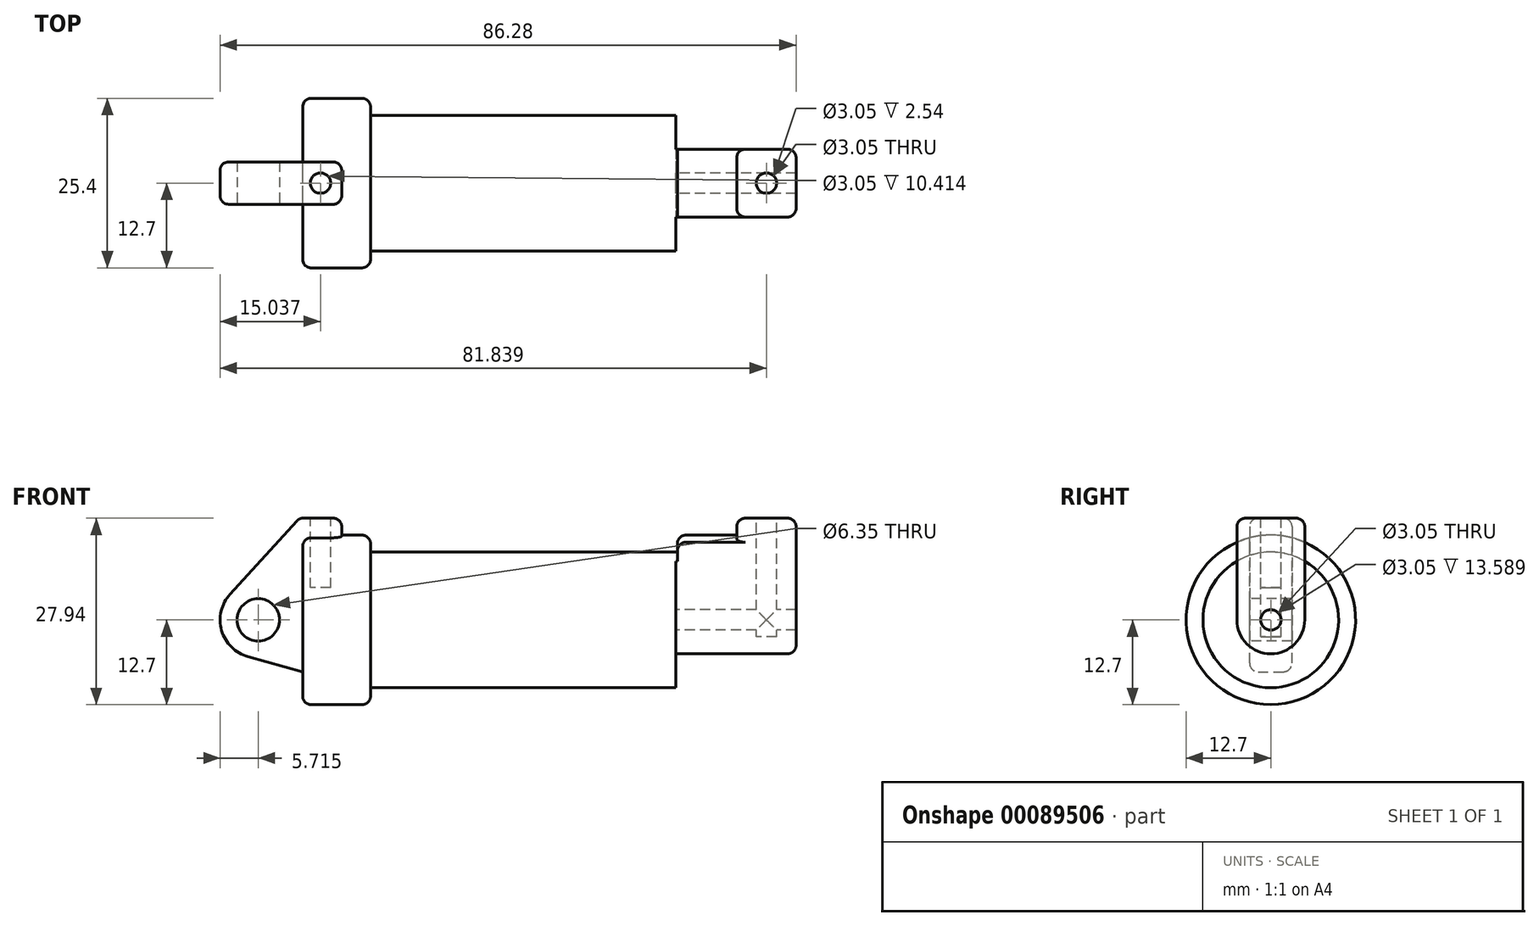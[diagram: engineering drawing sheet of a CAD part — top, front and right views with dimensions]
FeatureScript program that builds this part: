
annotation { "Feature Type Name" : "Feature", "Feature Type Description" : "" }
export const myFeature = defineFeature(function(context is Context, id is Id, definition is map)
    precondition{}
    {
        {
            var Q0;
            Q0=qCreatedBy(makeId("Front.planeOp"),FACE);
            var sketch = newSketch(context, id + "F0", { "sketchPlane" : qUnion([Q0])});
            skLineSegment(sketch, "E0", {"start": v(0, 0) * mm, "end": v(0, 12.7) * mm});
            skLineSegment(sketch, "E1", {"start": v(0, 12.7) * mm, "end": v(10.16, 12.7) * mm});
            skLineSegment(sketch, "E2", {"start": v(10.16, 12.7) * mm, "end": v(10.16, 10.16) * mm});
            skLineSegment(sketch, "E3", {"start": v(10.16, 10.16) * mm, "end": v(56.13, 10.16) * mm});
            skLineSegment(sketch, "E4", {"start": v(56.13, 10.16) * mm, "end": v(56.13, 12.7) * mm});
            skLineSegment(sketch, "E5", {"start": v(56.13, 12.7) * mm, "end": v(66.3, 12.7) * mm});
            skLineSegment(sketch, "E6", {"start": v(66.3, 12.7) * mm, "end": v(66.3, 0) * mm});
            skLineSegment(sketch, "E7", {"start": v(66.3, 0) * mm, "end": v(0, 0) * mm});
            skLineSegment(sketch, "E8", {"start": v(5.84, 15.24) * mm, "end": v(-0.5, 15.24) * mm});
            skLineSegment(sketch, "E9", {"start": v(-0.5, 15.24) * mm, "end": v(-10.88, 3.85) * mm});
            skLineSegment(sketch, "E10", {"start": v(0, 0) * mm, "end": v(-6.65, 0) * mm});
            skCircle(sketch, "E11", {"center": v(-6.65, 0) * mm, "radius": 5.72 * mm});
            skCircle(sketch, "E12", {"center": v(-6.65, 0) * mm, "radius": 3.18 * mm});
            skLineSegment(sketch, "E13", {"start": v(5.84, 15.24) * mm, "end": v(5.84, -9.4) * mm});
            skLineSegment(sketch, "E14", {"start": v(5.84, -9.4) * mm, "end": v(-8.18, -5.5) * mm});
            skSolve(sketch);
        }
        {
            var Q0;
            {var subQ0=sQuery(id+"F0.wireOp",EDGE,"E0");Q0=makeQuery(id+"F0.imprint","IMPRINT",FACE,{"disambiguationData":[TD([[makeQuery(id+"F0.imprint","IMPRINT",EDGE,{"derivedFrom":subQ0}),-1.0]])]});}
            var Q1;
            {var subQ3=sQuery(id+"F0.wireOp",EDGE,"E0");Q1=makeQuery(id+"F0.imprint","IMPRINT",FACE,{"disambiguationData":[TD([[makeQuery(id+"F0.imprint","IMPRINT",EDGE,{"derivedFrom":subQ3}),1.0]])]});}
            var Q2;
            {var subQ0=sQuery(id+"F0.wireOp",EDGE,"E14");Q2=makeQuery(id+"F0.imprint","IMPRINT",FACE,{"disambiguationData":[TD([[makeQuery(id+"F0.imprint","IMPRINT",EDGE,{"derivedFrom":subQ0}),-1.0]])]});}
            var Q3;
            {var subQ4=sQuery(id+"F0.wireOp",EDGE,"E12");Q3=makeQuery(id+"F0.imprint","IMPRINT",FACE,{"disambiguationData":[TD([[makeQuery(id+"F0.imprint","IMPRINT",EDGE,{"derivedFrom":subQ4}),-1.0]])]});}
            extrude(context, id + "F1", {"entities" : qUnion([Q0, Q1, Q2, Q3]), "endBound" : BoundingType.SYMMETRIC, "oppositeDirection" : true, "depth" : 6.35 * mm});
        }
        {
            var Q0;
            {var subQ0=sQuery(id+"F0.wireOp",EDGE,"E2");Q0=makeQuery(id+"F0.imprint","IMPRINT",FACE,{"disambiguationData":[TD([[makeQuery(id+"F0.imprint","IMPRINT",EDGE,{"derivedFrom":subQ0}),-1.0]])]});}
            var Q1;
            {var subQ0=sQuery(id+"F0.wireOp",EDGE,"E0");Q1=makeQuery(id+"F0.imprint","IMPRINT",FACE,{"disambiguationData":[TD([[makeQuery(id+"F0.imprint","IMPRINT",EDGE,{"derivedFrom":subQ0}),-1.0]])]});}
            var Q2;
            Q2=sQuery(id+"F0.wireOp",EDGE,"E7");
            revolve(context, id + "F2", {"operationType" : NewBodyOperationType.ADD, "entities" : qUnion([Q0, Q1]), "axis" : qUnion([Q2]), "revolveType" : RevolveType.FULL});
        }
        {
            var Q0;
            Q0=makeQuery(id+"F2.opRevolve","SWEPT_FACE",FACE,{"disambiguationData":[OSD([sQuery(id+"F0.wireOp",EDGE,"E6")])]});
            var sketch = newSketch(context, id + "F3", { "sketchPlane" : qUnion([Q0])});
            skCircle(sketch, "E15", {"center": v(0, 0) * mm, "radius": 1.52 * mm});
            skCircle(sketch, "E16", {"center": v(0, 0) * mm, "radius": 5.08 * mm});
            skLineSegment(sketch, "E17", {"start": v(-5.08, 0) * mm, "end": v(-5.08, 15.24) * mm});
            skLineSegment(sketch, "E18", {"start": v(5.08, 0) * mm, "end": v(5.08, 15.24) * mm});
            skLineSegment(sketch, "E19", {"start": v(-5.08, 15.24) * mm, "end": v(5.08, 15.24) * mm});
            skSolve(sketch);
        }
        {
            var Q0;
            Q0 = qSketchRegion(id + "F3", true);
            extrude(context, id + "F4", {"entities" : qUnion([Q0]), "operationType" : NewBodyOperationType.ADD, "depth" : 7.62 * mm});
        }
        {
            var Q0;
            Q0 = qSketchRegion(id + "F3", true);
            extrude(context, id + "F5", {"entities" : qUnion([Q0]), "operationType" : NewBodyOperationType.ADD, "oppositeDirection" : true, "depth" : 1.27 * mm});
        }
        {
            var Q0;
            {var subQ0=sQuery(id+"F3.wireOp",EDGE,"E19");Q0=makeQuery(id+"F5.boolean.opBoolean","MERGE",FACE,{"derivedFrom":[makeQuery(id+"F4.opExtrude","SWEPT_FACE",FACE,{"disambiguationData":[OSD([subQ0])]}),makeQuery(id+"F5.opExtrude","SWEPT_FACE",FACE,{"disambiguationData":[OSD([subQ0])]})]});}
            var sketch = newSketch(context, id + "F6", { "sketchPlane" : qUnion([Q0])});
            skLineSegment(sketch, "E20", {"start": v(65.02, 0) * mm, "end": v(73.91, 0) * mm, "construction": true});
            skLineSegment(sketch, "E21", {"start": v(69.47, 5.08) * mm, "end": v(69.47, -5.08) * mm, "construction": true});
            skCircle(sketch, "E22", {"center": v(69.47, 0) * mm, "radius": 1.52 * mm});
            skSolve(sketch);
        }
        {
            var Q0;
            Q0=makeQuery(id+"F4.boolean.opBoolean","SPLIT",FACE,{"disambiguationData":[TD([makeQuery(id+"F4.opExtrude","SWEPT_FACE",FACE,{"disambiguationData":[OSD([sQuery(id+"F3.wireOp",EDGE,"E15")])]})])],"derivedFrom":makeQuery(id+"F2.opRevolve","SWEPT_FACE",FACE,{"disambiguationData":[OSD([sQuery(id+"F0.wireOp",EDGE,"E6")])]})});
            extrude(context, id + "F7", {"entities" : qUnion([Q0]), "operationType" : NewBodyOperationType.ADD, "oppositeDirection" : true, "depth" : 10.4 * mm});
        }
        {
            var Q0;
            Q0=makeQuery(id+"F6.imprint","IMPRINT",FACE,{"disambiguationData":[TD([[makeQuery(id+"F6.imprint","IMPRINT",EDGE,{"derivedFrom":sQuery(id+"F6.wireOp",EDGE,"E22")}),1.0]])]});
            extrude(context, id + "F8", {"entities" : qUnion([Q0]), "operationType" : NewBodyOperationType.REMOVE, "oppositeDirection" : true, "depth" : 17.78 * mm});
        }
        {
            var Q0;
            Q0=makeQuery(id+"F4.boolean.opBoolean","SPLIT",FACE,{"disambiguationData":[TD([makeQuery(id+"F4.opExtrude","SWEPT_FACE",FACE,{"disambiguationData":[OSD([sQuery(id+"F3.wireOp",EDGE,"E15")])]})])],"derivedFrom":makeQuery(id+"F2.opRevolve","SWEPT_FACE",FACE,{"disambiguationData":[OSD([sQuery(id+"F0.wireOp",EDGE,"E6")])]})});
            extrude(context, id + "F9", {"entities" : qUnion([Q0]), "operationType" : NewBodyOperationType.REMOVE, "oppositeDirection" : true, "depth" : 10.4 * mm});
        }
        {
            var Q0;
            Q0=makeQuery(id+"F1.opExtrude","SWEPT_FACE",FACE,{"disambiguationData":[OSD([sQuery(id+"F0.wireOp",EDGE,"E8")])]});
            var sketch = newSketch(context, id + "F10", { "sketchPlane" : qUnion([Q0])});
            skLineSegment(sketch, "E23", {"start": v(2.67, 3.18) * mm, "end": v(2.67, -3.18) * mm, "construction": true});
            skLineSegment(sketch, "E24", {"start": v(-0.5, 0) * mm, "end": v(5.84, 0) * mm, "construction": true});
            skCircle(sketch, "E25", {"center": v(2.67, 0) * mm, "radius": 1.52 * mm});
            skSolve(sketch);
        }
        {
            var Q0;
            Q0 = qSketchRegion(id + "F10", true);
            extrude(context, id + "F11", {"entities" : qUnion([Q0]), "operationType" : NewBodyOperationType.REMOVE, "oppositeDirection" : true, "depth" : 10.4 * mm});
        }
        {
            var Q0;
            Q0=makeQuery(id+"F2.opRevolve","SWEPT_EDGE",EDGE,{"disambiguationData":[OSD([sQuery(id+"F0.wireOp",EDGE,"E1"),sQuery(id+"F0.wireOp",EDGE,"E2")])]});
            var Q1;
            Q1=makeQuery(id+"F2.opRevolve","SWEPT_EDGE",EDGE,{"disambiguationData":[OSD([sQuery(id+"F0.wireOp",EDGE,"E0"),sQuery(id+"F0.wireOp",EDGE,"E1")])]});
            var Q2;
            Q2=makeQuery(id+"F4.boolean.opBoolean","SPLIT",EDGE,{"disambiguationData":[OD(1.0)],"derivedFrom":makeQuery(id+"F2.opRevolve","SWEPT_EDGE",EDGE,{"disambiguationData":[OSD([sQuery(id+"F0.wireOp",EDGE,"E5"),sQuery(id+"F0.wireOp",EDGE,"E6")])]})});
            var Q3;
            Q3=makeQuery(id+"F2.opRevolve","SWEPT_EDGE",EDGE,{"disambiguationData":[OSD([sQuery(id+"F0.wireOp",EDGE,"E4"),sQuery(id+"F0.wireOp",EDGE,"E5")])]});
            fillet(context, id + "F12", {"entities" : qUnion([Q0, Q1, Q2, Q3]), "radius" : 1.27 * mm, "tangentPropagation" : true, "allowEdgeOverflow" : false});
        }
        {
            var Q0;
            {var subQ0=sQuery(id+"F3.wireOp",EDGE,"E19");var subQ1=sQuery(id+"F3.wireOp",EDGE,"E17");Q0=makeQuery(id+"F5.boolean.opBoolean","MERGE",EDGE,{"derivedFrom":[makeQuery(id+"F4.opExtrude","SWEPT_EDGE",EDGE,{"disambiguationData":[OSD([subQ1,subQ0])]}),makeQuery(id+"F5.opExtrude","SWEPT_EDGE",EDGE,{"disambiguationData":[OSD([subQ1,subQ0])]})]});}
            var Q1;
            Q1=makeQuery(id+"F4.opExtrude","CAP_EDGE",EDGE,{"disambiguationData":[OSD([sQuery(id+"F3.wireOp",EDGE,"E19")])],"isStart":false});
            var Q2;
            Q2=makeQuery(id+"F5.opExtrude","CAP_EDGE",EDGE,{"disambiguationData":[OSD([sQuery(id+"F3.wireOp",EDGE,"E19")])],"isStart":false});
            var Q3;
            {var subQ0=sQuery(id+"F3.wireOp",EDGE,"E19");var subQ1=sQuery(id+"F3.wireOp",EDGE,"E18");Q3=makeQuery(id+"F5.boolean.opBoolean","MERGE",EDGE,{"derivedFrom":[makeQuery(id+"F4.opExtrude","SWEPT_EDGE",EDGE,{"disambiguationData":[OSD([subQ1,subQ0])]}),makeQuery(id+"F5.opExtrude","SWEPT_EDGE",EDGE,{"disambiguationData":[OSD([subQ1,subQ0])]})]});}
            var Q4;
            Q4=makeQuery(id+"F4.opExtrude","CAP_EDGE",EDGE,{"disambiguationData":[OSD([sQuery(id+"F3.wireOp",EDGE,"E18")])],"isStart":false});
            var Q5;
            Q5=makeQuery(id+"F5.opExtrude","CAP_EDGE",EDGE,{"disambiguationData":[OSD([sQuery(id+"F3.wireOp",EDGE,"E18")])],"isStart":false});
            var Q6;
            Q6=makeQuery(id+"F5.opExtrude","CAP_EDGE",EDGE,{"disambiguationData":[OSD([sQuery(id+"F3.wireOp",EDGE,"E17")])],"isStart":false});
            fillet(context, id + "F13", {"entities" : qUnion([Q0, Q1, Q2, Q3, Q4, Q5, Q6]), "radius" : 1.27 * mm, "tangentPropagation" : true, "allowEdgeOverflow" : false});
        }
        {
            var Q0;
            Q0=makeQuery(id+"F1.opExtrude","CAP_EDGE",EDGE,{"disambiguationData":[OSD([sQuery(id+"F0.wireOp",EDGE,"E9")])],"isStart":true});
            var Q1;
            Q1=makeQuery(id+"F1.opExtrude","CAP_EDGE",EDGE,{"disambiguationData":[OSD([sQuery(id+"F0.wireOp",EDGE,"E9")])],"isStart":false});
            var Q2;
            Q2=makeQuery(id+"F1.opExtrude","CAP_EDGE",EDGE,{"disambiguationData":[OSD([sQuery(id+"F0.wireOp",EDGE,"E8")])],"isStart":true});
            var Q3;
            Q3=makeQuery(id+"F1.opExtrude","SWEPT_EDGE",EDGE,{"disambiguationData":[OSD([sQuery(id+"F0.wireOp",EDGE,"E8"),sQuery(id+"F0.wireOp",EDGE,"E9")])]});
            var Q4;
            Q4=makeQuery(id+"F1.opExtrude","CAP_EDGE",EDGE,{"disambiguationData":[OSD([sQuery(id+"F0.wireOp",EDGE,"E8")])],"isStart":false});
            var Q5;
            Q5=makeQuery(id+"F1.opExtrude","SWEPT_EDGE",EDGE,{"disambiguationData":[OSD([sQuery(id+"F0.wireOp",EDGE,"E8"),sQuery(id+"F0.wireOp",EDGE,"E13")])]});
            var Q6;
            Q6=makeQuery(id+"F1.opExtrude","CAP_EDGE",EDGE,{"disambiguationData":[OSD([sQuery(id+"F0.wireOp",EDGE,"E13")])],"isStart":true});
            var Q7;
            Q7=makeQuery(id+"F1.opExtrude","CAP_EDGE",EDGE,{"disambiguationData":[OSD([sQuery(id+"F0.wireOp",EDGE,"E11")])],"isStart":true});
            fillet(context, id + "F14", {"entities" : qUnion([Q0, Q1, Q2, Q3, Q4, Q5, Q6, Q7]), "radius" : 1.27 * mm, "tangentPropagation" : true, "allowEdgeOverflow" : false});
        }
        {
            var Q0;
            Q0=makeQuery(id+"F1.opExtrude","CAP_EDGE",EDGE,{"disambiguationData":[OSD([sQuery(id+"F0.wireOp",EDGE,"E13")])],"isStart":false});
            fillet(context, id + "F15", {"entities" : qUnion([Q0]), "radius" : 1.27 * mm, "tangentPropagation" : true, "allowEdgeOverflow" : false});
        }
    });
